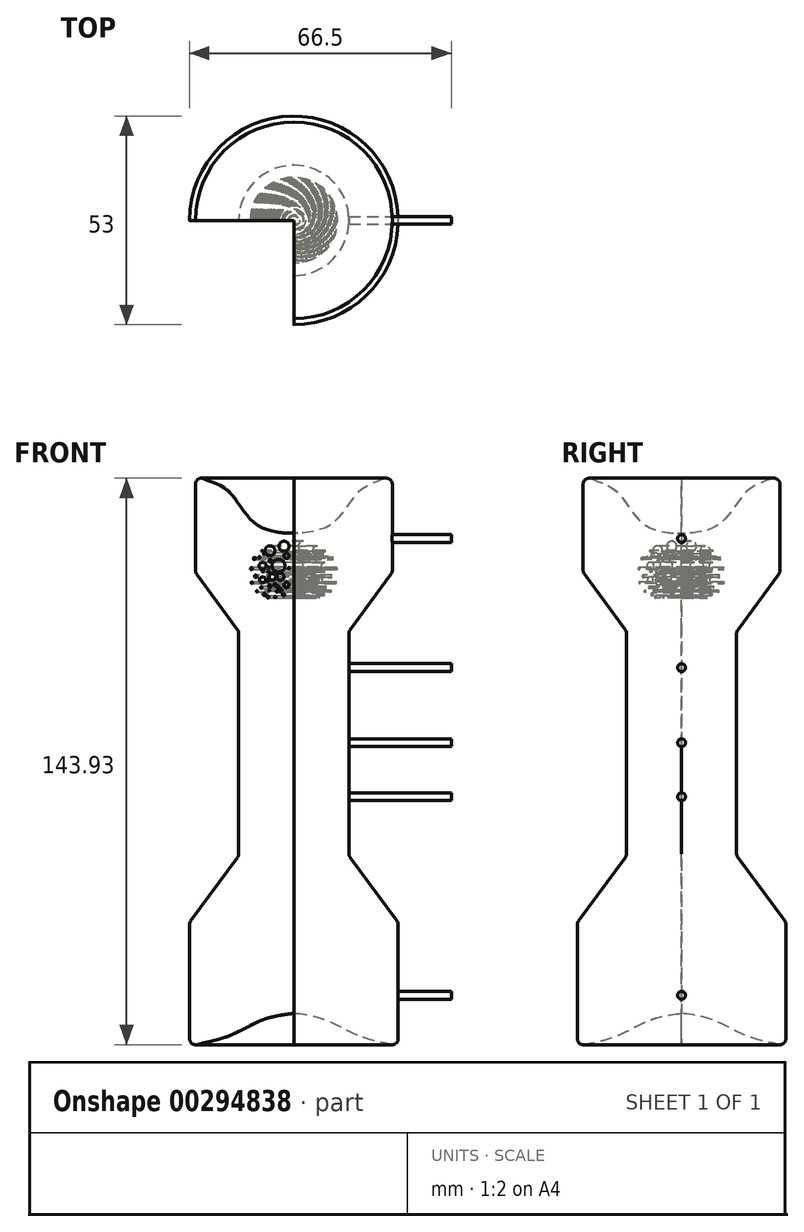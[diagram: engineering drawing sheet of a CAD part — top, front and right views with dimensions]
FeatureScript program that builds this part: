
annotation { "Feature Type Name" : "Feature", "Feature Type Description" : "" }
export const myFeature = defineFeature(function(context is Context, id is Id, definition is map)
    precondition{}
    {
        {
            var Q0;
            Q0=qCreatedBy(makeId("Front.planeOp"),FACE);
            var sketch = newSketch(context, id + "F0", { "sketchPlane" : qUnion([Q0])});
            skLineSegment(sketch, "E0", {"start": v(-26.5, 1.5) * mm, "end": v(-26.5, 30.5) * mm});
            skLineSegment(sketch, "E1", {"start": v(-26.2, 31.4) * mm, "end": v(-14.3, 47.6) * mm});
            skLineSegment(sketch, "E2", {"start": v(-14, 48.5) * mm, "end": v(-14, 104.5) * mm});
            skLineSegment(sketch, "E3", {"start": v(-14.3, 105.4) * mm, "end": v(-24.7, 119.6) * mm});
            skLineSegment(sketch, "E4", {"start": v(-25, 120.5) * mm, "end": v(-25, 142.43) * mm});
            skLineSegment(sketch, "E5", {"start": v(0, 130) * mm, "end": v(0, 7.98) * mm});
            skPoint(sketch, "E6.visualSharp", {"position": v(-25, 77.77) * mm});
            skFitSpline(sketch, "E7", {"points": [v(-25, 145) * mm, v(-16.99, 140.94) * mm, v(-9.43, 132.13) * mm, v(0, 130) * mm], "startDerivative": vector(20.03, -15.94) * mm, "endDerivative": vector(20.73, 1.21) * mm});
            skArc(sketch, "E8.filletArc", {"start": v(-22.9, 143.8) * mm, "mid": v(-24.32, 143.68) * mm, "end": v(-25, 142.43) * mm});
            skPoint(sketch, "E9.visualSharp", {"position": v(-25, 120) * mm});
            skArc(sketch, "E9.filletArc", {"start": v(-25, 120.5) * mm, "mid": v(-24.93, 120.02) * mm, "end": v(-24.7, 119.6) * mm});
            skPoint(sketch, "E10.visualSharp", {"position": v(-14, 105) * mm});
            skArc(sketch, "E10.filletArc", {"start": v(-14, 104.5) * mm, "mid": v(-14.07, 104.98) * mm, "end": v(-14.3, 105.4) * mm});
            skPoint(sketch, "E11.visualSharp", {"position": v(-14, 48) * mm});
            skArc(sketch, "E11.filletArc", {"start": v(-14.3, 47.6) * mm, "mid": v(-14.07, 48.02) * mm, "end": v(-14, 48.5) * mm});
            skPoint(sketch, "E12.visualSharp", {"position": v(-26.5, 31) * mm});
            skArc(sketch, "E12.filletArc", {"start": v(-26.2, 31.4) * mm, "mid": v(-26.43, 30.98) * mm, "end": v(-26.5, 30.5) * mm});
            skPoint(sketch, "E13.visualSharp", {"position": v(-26.5, 0) * mm});
            skArc(sketch, "E13.filletArc", {"start": v(-26.5, 1.5) * mm, "mid": v(-26.06, 0.44) * mm, "end": v(-25, 0) * mm});
            skFitSpline(sketch, "E14", {"points": [v(-25, 0) * mm, v(-15.8, 2.5) * mm, v(-8.07, 6.26) * mm, v(0, 7.98) * mm], "startDerivative": vector(27.44, 5.64) * mm, "endDerivative": vector(25.58, 3.45) * mm});
            skSolve(sketch);
        }
        {
            var Q0;
            Q0 = qSketchRegion(id + "F0", true);
            var Q1;
            Q1=sQuery(id+"F0.wireOp",EDGE,"E5");
            revolve(context, id + "F1", {"entities" : qUnion([Q0]), "axis" : qUnion([Q1]), "revolveType" : RevolveType.ONE_DIRECTION, "angle" : 270 * degree});
        }
        {
            var Q0;
            Q0=qCreatedBy(makeId("Right.planeOp"),FACE);
            var sketch = newSketch(context, id + "F2", { "sketchPlane" : qUnion([Q0])});
            skCircle(sketch, "E15", {"center": v(-2.5, 126.64) * mm, "radius": 1.27 * mm});
            skCircle(sketch, "E16", {"center": v(-6.07, 125.5) * mm, "radius": 1.26 * mm});
            skCircle(sketch, "E17", {"center": v(-3.9, 121.67) * mm, "radius": 1.63 * mm});
            skCircle(sketch, "E18", {"center": v(-7.94, 121.67) * mm, "radius": 0.89 * mm});
            skCircle(sketch, "E19", {"center": v(-7.94, 118.1) * mm, "radius": 0.74 * mm});
            skCircle(sketch, "E20", {"center": v(-3.4, 118.86) * mm, "radius": 0.9 * mm});
            skCircle(sketch, "E21", {"center": v(-5.43, 118.86) * mm, "radius": 0.85 * mm});
            skCircle(sketch, "E22", {"center": v(-1.86, 116.82) * mm, "radius": 0.69 * mm});
            skCircle(sketch, "E23", {"center": v(-1.86, 124.22) * mm, "radius": 0.65 * mm});
            skCircle(sketch, "E24", {"center": v(-4.14, 116.45) * mm, "radius": 0.28 * mm});
            skCircle(sketch, "E25", {"center": v(-4.8, 116.88) * mm, "radius": 0.28 * mm});
            skCircle(sketch, "E26", {"center": v(-3.33, 115.46) * mm, "radius": 0.4 * mm});
            skCircle(sketch, "E27", {"center": v(-1.3, 121.03) * mm, "radius": 0.17 * mm});
            skCircle(sketch, "E28", {"center": v(-5.96, 122.93) * mm, "radius": 0.35 * mm});
            skCircle(sketch, "E29", {"center": v(-8.75, 123.79) * mm, "radius": 0.2 * mm});
            skCircle(sketch, "E30", {"center": v(-10.78, 120.92) * mm, "radius": 0.25 * mm});
            skCircle(sketch, "E31", {"center": v(-7.89, 120.36) * mm, "radius": 0.25 * mm});
            skCircle(sketch, "E32", {"center": v(-6.39, 121.19) * mm, "radius": 0.19 * mm});
            skCircle(sketch, "E33", {"center": v(-6.44, 120.12) * mm, "radius": 0.19 * mm});
            skCircle(sketch, "E34", {"center": v(-6.55, 117.92) * mm, "radius": 0.22 * mm});
            skCircle(sketch, "E35", {"center": v(-6.15, 116.5) * mm, "radius": 0.34 * mm});
            skCircle(sketch, "E36", {"center": v(-8.26, 116.15) * mm, "radius": 0.2 * mm});
            skCircle(sketch, "E37", {"center": v(-6.25, 115.43) * mm, "radius": 0.15 * mm});
            skCircle(sketch, "E38", {"center": v(-4.27, 115.21) * mm, "radius": 0.2 * mm});
            skCircle(sketch, "E39", {"center": v(-2.61, 114.28) * mm, "radius": 0.27 * mm});
            skCircle(sketch, "E40", {"center": v(-4.73, 113.71) * mm, "radius": 0.16 * mm});
            skCircle(sketch, "E41", {"center": v(-6.6, 113.77) * mm, "radius": 0.26 * mm});
            skCircle(sketch, "E42", {"center": v(-7.49, 114.38) * mm, "radius": 0.31 * mm});
            skCircle(sketch, "E43", {"center": v(-9.39, 115.19) * mm, "radius": 0.16 * mm});
            skCircle(sketch, "E44", {"center": v(-10.68, 117.39) * mm, "radius": 0.17 * mm});
            skCircle(sketch, "E45", {"center": v(-9.71, 119) * mm, "radius": 0.3 * mm});
            skCircle(sketch, "E46", {"center": v(-10.03, 123.5) * mm, "radius": 0.28 * mm});
            skCircle(sketch, "E47", {"center": v(-8.08, 125.47) * mm, "radius": 0.13 * mm});
            skCircle(sketch, "E48", {"center": v(-7.6, 124.77) * mm, "radius": 0.15 * mm});
            skSolve(sketch);
        }
        {
            var Q0;
            Q0 = qSketchRegion(id + "F2", true);
            var Q1;
            Q1=makeQuery(id+"F1.opRevolve","CAP_EDGE",EDGE,{"disambiguationData":[OSD([sQuery(id+"F0.wireOp",EDGE,"E5")])],"isStart":true});
            revolve(context, id + "F3", {"operationType" : NewBodyOperationType.REMOVE, "entities" : qUnion([Q0]), "axis" : qUnion([Q1]), "revolveType" : RevolveType.FULL, "oppositeDirection" : true});
        }
        {
            var Q0;
            Q0=qCreatedBy(makeId("Right.planeOp"),FACE);
            cPlane(context, id + "F4", {"entities" : qUnion([Q0]), "cplaneType" : CPlaneType.OFFSET, "offset" : 40 * mm, "width" : 150 * mm, "height" : 150 * mm});
        }
        {
            var Q0;
            Q0=qCreatedBy(id+"F4.planeOp",FACE);
            var sketch = newSketch(context, id + "F5", { "sketchPlane" : qUnion([Q0])});
            skCircle(sketch, "E49", {"center": v(0, 12.54) * mm, "radius": 1 * mm});
            skCircle(sketch, "E50", {"center": v(0, 63) * mm, "radius": 1 * mm});
            skCircle(sketch, "E51", {"center": v(0, 76.71) * mm, "radius": 1 * mm});
            skCircle(sketch, "E52", {"center": v(0, 95.8) * mm, "radius": 1 * mm});
            skCircle(sketch, "E53", {"center": v(0, 128.59) * mm, "radius": 1 * mm});
            skSolve(sketch);
        }
        {
            var Q0;
            Q0 = qSketchRegion(id + "F5", true);
            extrude(context, id + "F6", {"entities" : qUnion([Q0]), "operationType" : NewBodyOperationType.ADD, "oppositeDirection" : true, "depth" : 30 * mm});
        }
    });
